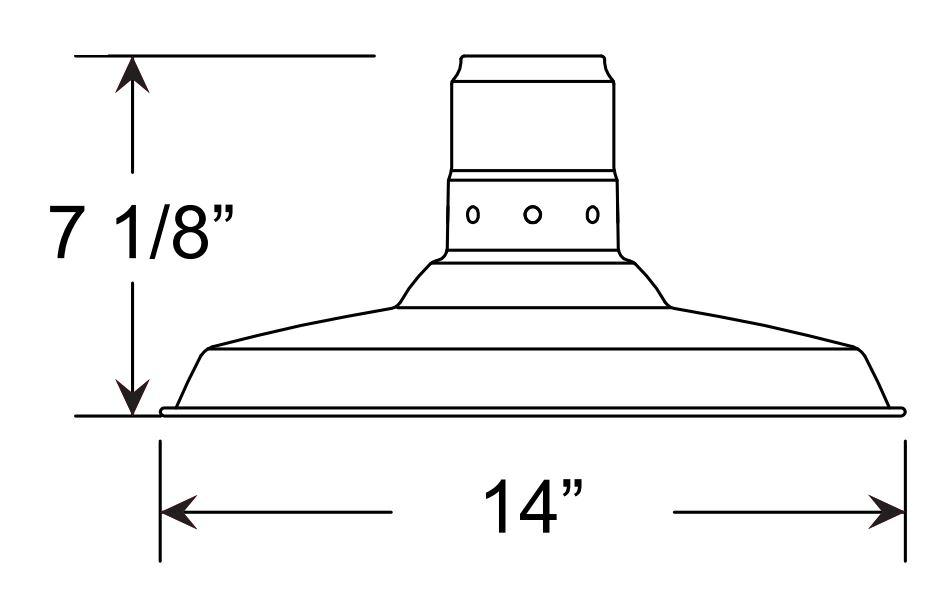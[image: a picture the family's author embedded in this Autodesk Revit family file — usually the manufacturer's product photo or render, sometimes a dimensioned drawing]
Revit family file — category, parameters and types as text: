
# Revit family: Warehouse Flat MB 20,24,27
name_source: partatom
category: Lighting Fixtures
units: mm (PartAtom-declared; Revit-internal decimal feet)

## family parameters
Always vertical = Yes
Cut with Voids When Loaded = No
Light Source = Yes
OmniClass Number = 23.80.70.00
OmniClass Title = Lighting
Part Type = Normal
Room Calculation Point = No
Round Connector Dimension = Use Diameter
Shared = No
Work Plane-Based = No

## types (3) — shared parameters
Apparent Load = 200 VA
BULB = Yes
Body Colour = Spun aluminium
Body Material = body
Bulb = Bulb
CRI = >90
Canopy Body = Textured Black
Color Filter = 16777215
Construction Material = Heavy Duty spun aluminum.
Default Elevation = 0' - 0"
Description = 120-277 Voltage
Dimming = 1%
Dimming Lamp Color Temperature Shift = <None>
Efficiency = 65-125 lumens per watt
Lamp = MB
Life = L70 50,000 hours
Load Classification = Lighting
Manufacturer = ANP Lighting
Photometric Web File = generic
Power Factor = 1
Tilt Angle = 90.00°
URL = https://www.anplighting.com
Voltage = 120 V
Warranty = 5 year limited warranty
Wattage Comments = 200 W Max
b = 0' - 2"

## per-type parameters (varying)
| type | Fixture Diameter | Fixture Height | WF520 | WF524 | WF527 | Weight | a |
| WF520 | 1' - 8" | 0' - 6" | Yes | No | No | 2.5 lb | 0' - 6" |
| WF524 | 2' - 0" | 0' - 6 3/4" | No | Yes | No | 5.5 lb | 0' - 6 3/4" |
| WF527 | 2' - 3" | 0' - 7 3/4" | No | No | Yes | 6.0 lb | 0' - 7 3/4" |

note: column(s) folded — value = type name in every type: Model

## geometry (parser evidence)
native form markers: Sweep x21
no freeform markers — native parametric forms only
